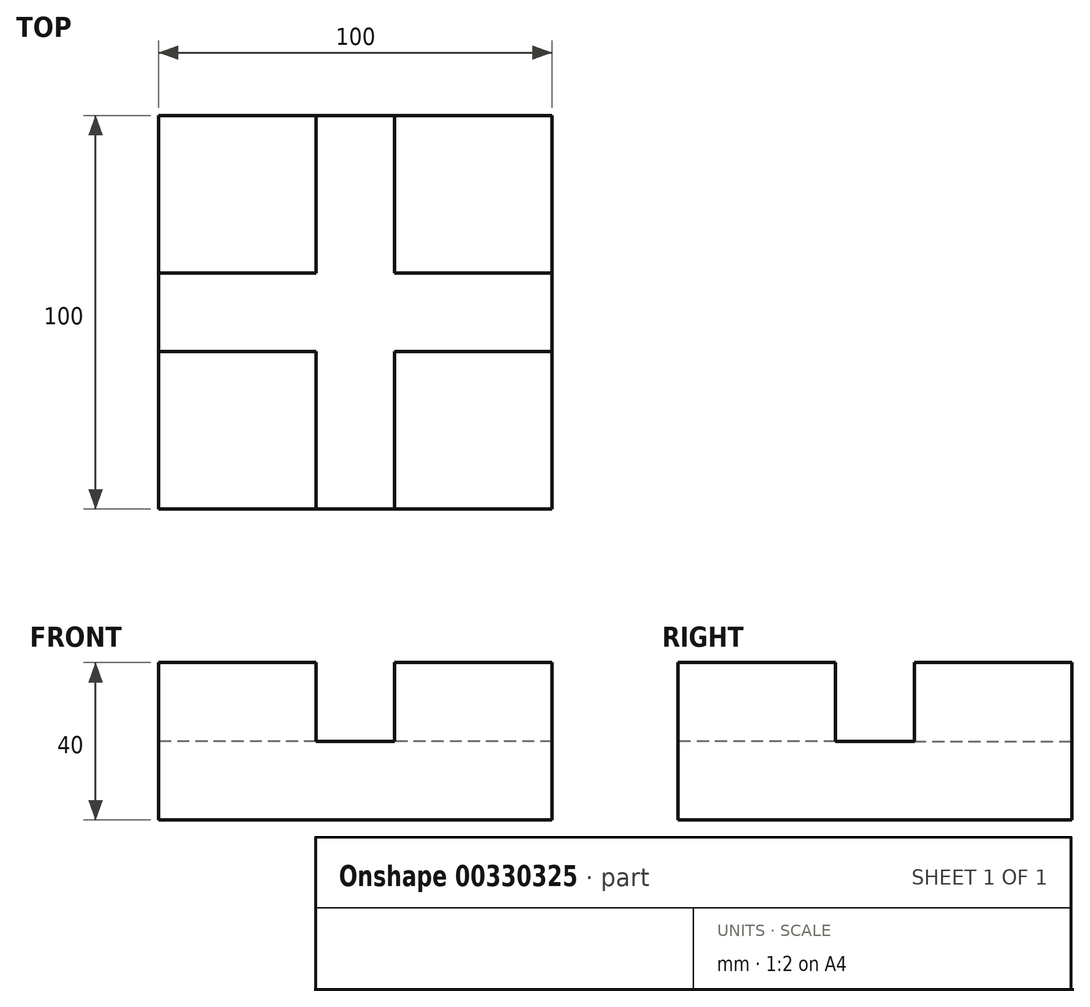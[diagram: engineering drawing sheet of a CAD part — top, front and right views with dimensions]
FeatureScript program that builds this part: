
annotation { "Feature Type Name" : "Feature", "Feature Type Description" : "" }
export const myFeature = defineFeature(function(context is Context, id is Id, definition is map)
    precondition{}
    {
        {
            var Q0;
            Q0=qCreatedBy(makeId("Top.planeOp"),FACE);
            var sketch = newSketch(context, id + "F0", { "sketchPlane" : qUnion([Q0])});
            skLineSegment(sketch, "E0.bottom", {"start": v(-78.35, 62.78) * mm, "end": v(21.65, 62.78) * mm});
            skLineSegment(sketch, "E0.top", {"start": v(-78.35, -37.22) * mm, "end": v(21.65, -37.22) * mm});
            skLineSegment(sketch, "E0.left", {"start": v(-78.35, 62.78) * mm, "end": v(-78.35, -37.22) * mm});
            skLineSegment(sketch, "E0.right", {"start": v(21.65, 62.78) * mm, "end": v(21.65, -37.22) * mm});
            skSolve(sketch);
        }
        {
            var Q0;
            Q0 = qSketchRegion(id + "F0", true);
            extrude(context, id + "F1", {"entities" : qUnion([Q0]), "depth" : 40 * mm});
        }
        {
            var Q0;
            Q0=makeQuery(id+"F1.opExtrude","CAP_FACE",FACE,{"disambiguationData":[OSD([sQuery(id+"F0.wireOp",EDGE,"E0.bottom"),sQuery(id+"F0.wireOp",EDGE,"E0.top"),sQuery(id+"F0.wireOp",EDGE,"E0.left"),sQuery(id+"F0.wireOp",EDGE,"E0.right")])],"isStart":false});
            var sketch = newSketch(context, id + "F2", { "sketchPlane" : qUnion([Q0])});
            skLineSegment(sketch, "E1.bottom", {"start": v(-78.35, 62.78) * mm, "end": v(-38.35, 62.78) * mm, "construction": true});
            skLineSegment(sketch, "E1.top", {"start": v(-78.35, -37.22) * mm, "end": v(-38.35, -37.22) * mm, "construction": true});
            skLineSegment(sketch, "E1.left", {"start": v(-78.35, 62.78) * mm, "end": v(-78.35, 22.78) * mm, "construction": true});
            skLineSegment(sketch, "E1.right", {"start": v(21.65, 62.78) * mm, "end": v(21.65, 22.78) * mm, "construction": true});
            skLineSegment(sketch, "E2", {"start": v(-28.35, 62.78) * mm, "end": v(-28.35, -37.22) * mm, "construction": true});
            skLineSegment(sketch, "E3", {"start": v(-78.35, 12.78) * mm, "end": v(21.65, 12.78) * mm, "construction": true});
            skLineSegment(sketch, "E4", {"start": v(-38.35, 62.78) * mm, "end": v(-38.35, 22.78) * mm});
            skLineSegment(sketch, "E5", {"start": v(-18.35, -37.22) * mm, "end": v(-18.35, 2.78) * mm});
            skLineSegment(sketch, "E6", {"start": v(21.65, 22.78) * mm, "end": v(-18.35, 22.78) * mm});
            skLineSegment(sketch, "E7", {"start": v(-78.35, 2.78) * mm, "end": v(-38.35, 2.78) * mm});
            skLineSegment(sketch, "E8", {"start": v(-38.35, -37.22) * mm, "end": v(-18.35, -37.22) * mm});
            skLineSegment(sketch, "E9", {"start": v(-18.35, -37.22) * mm, "end": v(21.65, -37.22) * mm, "construction": true});
            skLineSegment(sketch, "E10", {"start": v(21.65, 2.78) * mm, "end": v(21.65, -37.22) * mm, "construction": true});
            skLineSegment(sketch, "E11", {"start": v(21.65, 22.78) * mm, "end": v(21.65, 2.78) * mm});
            skLineSegment(sketch, "E12", {"start": v(-78.35, 2.78) * mm, "end": v(-78.35, -37.22) * mm, "construction": true});
            skLineSegment(sketch, "E13", {"start": v(-78.35, 22.78) * mm, "end": v(-78.35, 2.78) * mm});
            skLineSegment(sketch, "E14", {"start": v(-18.35, 62.78) * mm, "end": v(21.65, 62.78) * mm, "construction": true});
            skLineSegment(sketch, "E15", {"start": v(-38.35, 62.78) * mm, "end": v(-18.35, 62.78) * mm});
            skLineSegment(sketch, "E16", {"start": v(-18.35, 22.78) * mm, "end": v(-18.35, 62.78) * mm});
            skLineSegment(sketch, "E17", {"start": v(-38.35, 22.78) * mm, "end": v(-78.35, 22.78) * mm});
            skLineSegment(sketch, "E18", {"start": v(-38.35, 2.78) * mm, "end": v(-18.35, 2.78) * mm, "construction": true});
            skLineSegment(sketch, "E19", {"start": v(-18.35, 2.78) * mm, "end": v(21.65, 2.78) * mm});
            skLineSegment(sketch, "E20", {"start": v(-18.35, 2.78) * mm, "end": v(-18.35, 22.78) * mm, "construction": true});
            skLineSegment(sketch, "E21", {"start": v(-18.35, 22.78) * mm, "end": v(-38.35, 22.78) * mm, "construction": true});
            skLineSegment(sketch, "E22", {"start": v(-38.35, 2.78) * mm, "end": v(-38.35, -37.22) * mm});
            skLineSegment(sketch, "E23", {"start": v(-38.35, 22.78) * mm, "end": v(-38.35, 2.78) * mm, "construction": true});
            skSolve(sketch);
        }
        {
            var Q0;
            Q0 = qSketchRegion(id + "F2", true);
            extrude(context, id + "F3", {"entities" : qUnion([Q0]), "operationType" : NewBodyOperationType.REMOVE, "oppositeDirection" : true, "depth" : 20 * mm});
        }
    });
